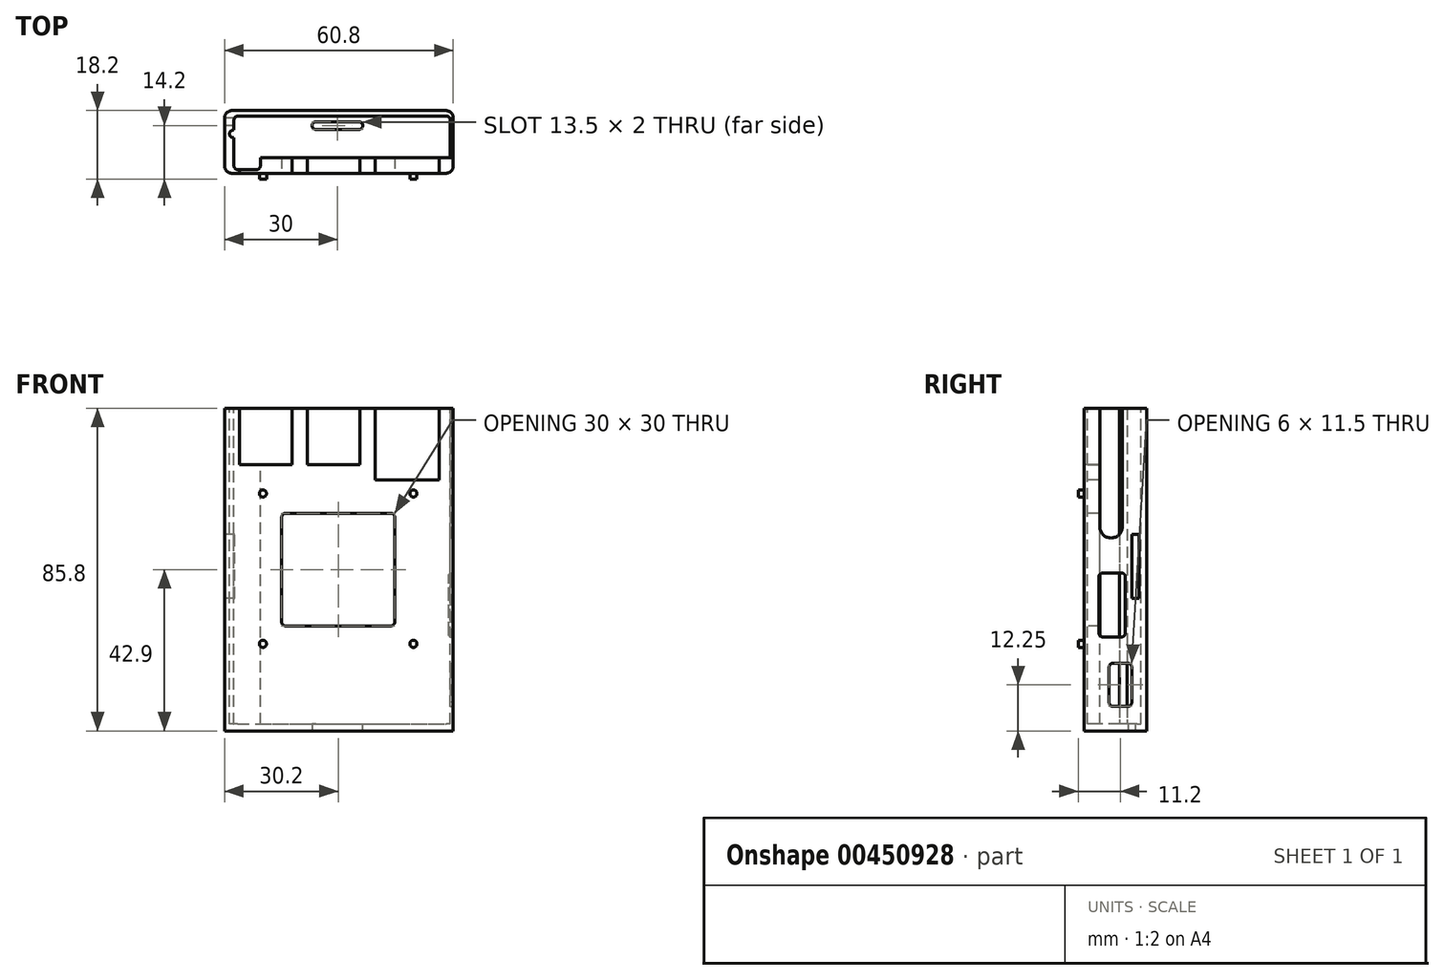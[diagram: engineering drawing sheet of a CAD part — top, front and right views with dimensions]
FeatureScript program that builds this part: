
annotation { "Feature Type Name" : "Feature", "Feature Type Description" : "" }
export const myFeature = defineFeature(function(context is Context, id is Id, definition is map)
    precondition{}
    {
        {
            var Q0;
            Q0=qCreatedBy(makeId("Top.planeOp"),FACE);
            var sketch = newSketch(context, id + "F0", { "sketchPlane" : qUnion([Q0])});
            skLineSegment(sketch, "E0.bottom", {"start": v(30.4, -8.35) * mm, "end": v(-30.4, -8.35) * mm});
            skLineSegment(sketch, "E0.top", {"start": v(30.4, 8.35) * mm, "end": v(-30.4, 8.35) * mm});
            skLineSegment(sketch, "E0.left", {"start": v(30.4, -8.35) * mm, "end": v(30.4, 8.35) * mm});
            skLineSegment(sketch, "E0.right", {"start": v(-30.4, -8.35) * mm, "end": v(-30.4, 8.35) * mm});
            skPoint(sketch, "E0.middle", {"position": v(0, 0) * mm});
            skSolve(sketch);
        }
        {
            var Q0;
            Q0=makeQuery(id+"F0.imprint","IMPRINT",FACE,{"disambiguationData":[TD([[makeQuery(id+"F0.imprint","IMPRINT",EDGE,{"derivedFrom":sQuery(id+"F0.wireOp",EDGE,"E0.bottom")}),-1.0]])]});
            extrude(context, id + "F1", {"entities" : qUnion([Q0]), "depth" : 85.8 * mm, "offsetDistance" : 25 * mm, "flatOperationType" : FlatOperationType.REMOVE, "domain" : OperationDomain.MODEL});
        }
        {
            var Q0;
            Q0=makeQuery(id+"F1.opExtrude","CAP_FACE",FACE,{"disambiguationData":[OSD([sQuery(id+"F0.wireOp",EDGE,"E0.bottom"),sQuery(id+"F0.wireOp",EDGE,"E0.top"),sQuery(id+"F0.wireOp",EDGE,"E0.left"),sQuery(id+"F0.wireOp",EDGE,"E0.right")])],"isStart":false});
            var sketch = newSketch(context, id + "F2", { "sketchPlane" : qUnion([Q0])});
            skLineSegment(sketch, "E1.bottom", {"start": v(-27.9, 6.85) * mm, "end": v(29.6, 6.85) * mm});
            skLineSegment(sketch, "E1.top", {"start": v(-27.9, -4.15) * mm, "end": v(29.6, -4.15) * mm});
            skLineSegment(sketch, "E1.left", {"start": v(-27.9, 6.85) * mm, "end": v(-27.9, -4.15) * mm});
            skLineSegment(sketch, "E1.right", {"start": v(29.6, 6.85) * mm, "end": v(29.6, -4.15) * mm});
            skSolve(sketch);
        }
        {
            var Q0;
            Q0=makeQuery(id+"F2.imprint","IMPRINT",FACE,{"disambiguationData":[TD([[makeQuery(id+"F2.imprint","IMPRINT",EDGE,{"derivedFrom":sQuery(id+"F2.wireOp",EDGE,"E1.bottom")}),-1.0]])]});
            extrude(context, id + "F3", {"entities" : qUnion([Q0]), "operationType" : NewBodyOperationType.REMOVE, "oppositeDirection" : true, "depth" : 84 * mm, "offsetDistance" : 25 * mm});
        }
        {
            var Q0;
            Q0=makeQuery(id+"F1.opExtrude","CAP_FACE",FACE,{"disambiguationData":[OSD([sQuery(id+"F0.wireOp",EDGE,"E0.bottom"),sQuery(id+"F0.wireOp",EDGE,"E0.top"),sQuery(id+"F0.wireOp",EDGE,"E0.left"),sQuery(id+"F0.wireOp",EDGE,"E0.right")])],"isStart":false});
            var sketch = newSketch(context, id + "F4", { "sketchPlane" : qUnion([Q0])});
            skLineSegment(sketch, "E2.bottom", {"start": v(-27.9, -4.15) * mm, "end": v(-20.9, -4.15) * mm});
            skLineSegment(sketch, "E2.top", {"start": v(-27.9, -7.35) * mm, "end": v(-20.9, -7.35) * mm});
            skLineSegment(sketch, "E2.left", {"start": v(-27.9, -4.15) * mm, "end": v(-27.9, -7.35) * mm});
            skLineSegment(sketch, "E2.right", {"start": v(-20.9, -4.15) * mm, "end": v(-20.9, -7.35) * mm});
            skSolve(sketch);
        }
        {
            var Q0;
            Q0 = qSketchRegion(id + "F4", true);
            extrude(context, id + "F5", {"entities" : qUnion([Q0]), "operationType" : NewBodyOperationType.REMOVE, "oppositeDirection" : true, "depth" : 84 * mm, "offsetDistance" : 25 * mm});
        }
        {
            var Q0;
            Q0=makeQuery(id+"F1.opExtrude","SWEPT_FACE",FACE,{"disambiguationData":[OSD([sQuery(id+"F0.wireOp",EDGE,"E0.bottom")])]});
            var sketch = newSketch(context, id + "F6", { "sketchPlane" : qUnion([Q0])});
            skLineSegment(sketch, "E3.bottom", {"start": v(-12.4, 70.8) * mm, "end": v(-26.4, 70.8) * mm});
            skLineSegment(sketch, "E3.top", {"start": v(-12.4, 85.8) * mm, "end": v(-26.4, 85.8) * mm});
            skLineSegment(sketch, "E3.left", {"start": v(-12.4, 70.8) * mm, "end": v(-12.4, 85.8) * mm});
            skLineSegment(sketch, "E3.right", {"start": v(-26.4, 70.8) * mm, "end": v(-26.4, 85.8) * mm});
            skPoint(sketch, "E3.middle", {"position": v(-19.4, 78.3) * mm});
            skSolve(sketch);
        }
        {
            var Q0;
            Q0=makeQuery(id+"F6.imprint","IMPRINT",FACE,{"disambiguationData":[TD([[makeQuery(id+"F6.imprint","IMPRINT",EDGE,{"derivedFrom":sQuery(id+"F6.wireOp",EDGE,"E3.bottom")}),1.0]])]});
            var sketch = newSketch(context, id + "F7", { "sketchPlane" : qUnion([Q0])});
            skLineSegment(sketch, "E4.bottom", {"start": v(5.6, 70.8) * mm, "end": v(-8.4, 70.8) * mm});
            skLineSegment(sketch, "E4.top", {"start": v(5.6, 85.8) * mm, "end": v(-8.4, 85.8) * mm});
            skLineSegment(sketch, "E4.left", {"start": v(5.6, 70.8) * mm, "end": v(5.6, 85.8) * mm});
            skLineSegment(sketch, "E4.right", {"start": v(-8.4, 70.8) * mm, "end": v(-8.4, 85.8) * mm});
            skPoint(sketch, "E4.middle", {"position": v(-1.4, 78.3) * mm});
            skSolve(sketch);
        }
        {
            var Q0;
            Q0=makeQuery(id+"F6.imprint","IMPRINT",FACE,{"disambiguationData":[TD([[makeQuery(id+"F6.imprint","IMPRINT",EDGE,{"derivedFrom":sQuery(id+"F6.wireOp",EDGE,"E3.bottom")}),1.0]])]});
            var sketch = newSketch(context, id + "F8", { "sketchPlane" : qUnion([Q0])});
            skLineSegment(sketch, "E5.bottom", {"start": v(26.6, 66.8) * mm, "end": v(9.6, 66.8) * mm});
            skLineSegment(sketch, "E5.top", {"start": v(26.6, 85.8) * mm, "end": v(9.6, 85.8) * mm});
            skLineSegment(sketch, "E5.left", {"start": v(26.6, 66.8) * mm, "end": v(26.6, 85.8) * mm});
            skLineSegment(sketch, "E5.right", {"start": v(9.6, 66.8) * mm, "end": v(9.6, 85.8) * mm});
            skPoint(sketch, "E5.middle", {"position": v(18.1, 76.3) * mm});
            skSolve(sketch);
        }
        {
            var Q0;
            Q0 = qSketchRegion(id + "F6", true);
            var Q1;
            Q1 = qSketchRegion(id + "F7", true);
            var Q2;
            Q2 = qSketchRegion(id + "F8", true);
            extrude(context, id + "F9", {"entities" : qUnion([Q0, Q1, Q2]), "operationType" : NewBodyOperationType.REMOVE, "oppositeDirection" : true, "depth" : 4.5 * mm, "offsetDistance" : 25 * mm});
        }
        {
            var Q0;
            Q0=makeQuery(id+"F1.opExtrude","SWEPT_FACE",FACE,{"disambiguationData":[OSD([sQuery(id+"F0.wireOp",EDGE,"E0.left")])]});
            var sketch = newSketch(context, id + "F10", { "sketchPlane" : qUnion([Q0])});
            skLineSegment(sketch, "E6.bottom", {"start": v(-1.65, 6.5) * mm, "end": v(4.35, 6.5) * mm});
            skLineSegment(sketch, "E6.top", {"start": v(-1.65, 18) * mm, "end": v(4.35, 18) * mm});
            skLineSegment(sketch, "E6.left", {"start": v(-1.65, 6.5) * mm, "end": v(-1.65, 18) * mm});
            skLineSegment(sketch, "E6.right", {"start": v(4.35, 6.5) * mm, "end": v(4.35, 18) * mm});
            skSolve(sketch);
        }
        {
            var Q0;
            Q0=makeQuery(id+"F10.imprint","IMPRINT",FACE,{"disambiguationData":[TD([[makeQuery(id+"F10.imprint","IMPRINT",EDGE,{"derivedFrom":sQuery(id+"F10.wireOp",EDGE,"E6.bottom")}),-1.0]])]});
            var sketch = newSketch(context, id + "F11", { "sketchPlane" : qUnion([Q0])});
            skLineSegment(sketch, "E7.bottom", {"start": v(-4.35, 25) * mm, "end": v(2.65, 25) * mm});
            skLineSegment(sketch, "E7.top", {"start": v(-4.35, 42) * mm, "end": v(2.65, 42) * mm});
            skLineSegment(sketch, "E7.left", {"start": v(-4.35, 25) * mm, "end": v(-4.35, 42) * mm});
            skLineSegment(sketch, "E7.right", {"start": v(2.65, 25) * mm, "end": v(2.65, 42) * mm});
            skSolve(sketch);
        }
        {
            var Q0;
            Q0=makeQuery(id+"F10.imprint","IMPRINT",FACE,{"disambiguationData":[TD([[makeQuery(id+"F10.imprint","IMPRINT",EDGE,{"derivedFrom":sQuery(id+"F10.wireOp",EDGE,"E6.bottom")}),-1.0]])]});
            var sketch = newSketch(context, id + "F12", { "sketchPlane" : qUnion([Q0])});
            skCircle(sketch, "E8", {"center": v(-1.15, 54.8) * mm, "radius": 2.5 * mm});
            skSolve(sketch);
        }
        {
            var Q0;
            Q0=makeQuery(id+"F3.boolean.opBoolean","COPY",FACE,{"derivedFrom":makeQuery(id+"F3.opExtrude","SWEPT_FACE",FACE,{"disambiguationData":[OSD([sQuery(id+"F2.wireOp",EDGE,"E1.right")])]})});
            var sketch = newSketch(context, id + "F13", { "sketchPlane" : qUnion([Q0])});
            skLineSegment(sketch, "E9.bottom", {"start": v(4.15, 85.8) * mm, "end": v(-1.85, 85.8) * mm});
            skLineSegment(sketch, "E9.top", {"start": v(4.15, 54.3) * mm, "end": v(-1.85, 54.3) * mm});
            skLineSegment(sketch, "E9.left", {"start": v(4.15, 85.8) * mm, "end": v(4.15, 54.3) * mm});
            skLineSegment(sketch, "E9.right", {"start": v(-1.85, 85.8) * mm, "end": v(-1.85, 54.3) * mm});
            skSolve(sketch);
        }
        {
            var Q0;
            Q0=makeQuery(id+"F13.imprint","IMPRINT",FACE,{"disambiguationData":[TD([[makeQuery(id+"F13.imprint","IMPRINT",EDGE,{"derivedFrom":sQuery(id+"F13.wireOp",EDGE,"E9.bottom")}),-1.0]])]});
            extrude(context, id + "F14", {"entities" : qUnion([Q0]), "operationType" : NewBodyOperationType.REMOVE, "oppositeDirection" : true, "depth" : 1.5 * mm, "offsetDistance" : 25 * mm});
        }
        {
            var Q0;
            Q0 = qSketchRegion(id + "F12", true);
            extrude(context, id + "F15", {"entities" : qUnion([Q0]), "operationType" : NewBodyOperationType.REMOVE, "oppositeDirection" : true, "depth" : 1.5 * mm, "offsetDistance" : 25 * mm});
        }
        {
            var Q0;
            Q0 = qSketchRegion(id + "F11", true);
            var Q1;
            Q1 = qSketchRegion(id + "F10", true);
            extrude(context, id + "F16", {"entities" : qUnion([Q0, Q1]), "operationType" : NewBodyOperationType.REMOVE, "oppositeDirection" : true, "depth" : 1.25 * mm, "offsetDistance" : 25 * mm});
        }
        {
            var Q0;
            Q0=makeQuery(id+"F3.boolean.opBoolean","COPY",FACE,{"derivedFrom":makeQuery(id+"F3.opExtrude","SWEPT_FACE",FACE,{"disambiguationData":[OSD([sQuery(id+"F2.wireOp",EDGE,"E1.right")])]})});
            var sketch = newSketch(context, id + "F17", { "sketchPlane" : qUnion([Q0])});
            skCircle(sketch, "E10", {"center": v(1.15, 54.3) * mm, "radius": 3 * mm});
            skSolve(sketch);
        }
        {
            var Q0;
            Q0 = qSketchRegion(id + "F17", true);
            extrude(context, id + "F18", {"entities" : qUnion([Q0]), "operationType" : NewBodyOperationType.REMOVE, "oppositeDirection" : true, "depth" : 1.8 * mm, "offsetDistance" : 25 * mm});
        }
        {
            var Q0;
            Q0=makeQuery(id+"F16.boolean.opBoolean","COPY",EDGE,{"derivedFrom":makeQuery(id+"F16.opExtrude","SWEPT_EDGE",EDGE,{"disambiguationData":[OSD([sQuery(id+"F11.wireOp",EDGE,"E7.bottom"),sQuery(id+"F11.wireOp",EDGE,"E7.left")])]})});
            var Q1;
            Q1=makeQuery(id+"F16.boolean.opBoolean","COPY",EDGE,{"derivedFrom":makeQuery(id+"F16.opExtrude","SWEPT_EDGE",EDGE,{"disambiguationData":[OSD([sQuery(id+"F11.wireOp",EDGE,"E7.top"),sQuery(id+"F11.wireOp",EDGE,"E7.left")])]})});
            var Q2;
            Q2=makeQuery(id+"F16.boolean.opBoolean","COPY",EDGE,{"derivedFrom":makeQuery(id+"F16.opExtrude","SWEPT_EDGE",EDGE,{"disambiguationData":[OSD([sQuery(id+"F10.wireOp",EDGE,"E6.top"),sQuery(id+"F10.wireOp",EDGE,"E6.left")])]})});
            var Q3;
            Q3=makeQuery(id+"F16.boolean.opBoolean","COPY",EDGE,{"derivedFrom":makeQuery(id+"F16.opExtrude","SWEPT_EDGE",EDGE,{"disambiguationData":[OSD([sQuery(id+"F11.wireOp",EDGE,"E7.top"),sQuery(id+"F11.wireOp",EDGE,"E7.right")])]})});
            var Q4;
            Q4=makeQuery(id+"F16.boolean.opBoolean","COPY",EDGE,{"derivedFrom":makeQuery(id+"F16.opExtrude","SWEPT_EDGE",EDGE,{"disambiguationData":[OSD([sQuery(id+"F11.wireOp",EDGE,"E7.bottom"),sQuery(id+"F11.wireOp",EDGE,"E7.right")])]})});
            var Q5;
            Q5=makeQuery(id+"F16.boolean.opBoolean","COPY",EDGE,{"derivedFrom":makeQuery(id+"F16.opExtrude","SWEPT_EDGE",EDGE,{"disambiguationData":[OSD([sQuery(id+"F10.wireOp",EDGE,"E6.top"),sQuery(id+"F10.wireOp",EDGE,"E6.right")])]})});
            var Q6;
            Q6=makeQuery(id+"F16.boolean.opBoolean","COPY",EDGE,{"derivedFrom":makeQuery(id+"F16.opExtrude","SWEPT_EDGE",EDGE,{"disambiguationData":[OSD([sQuery(id+"F10.wireOp",EDGE,"E6.bottom"),sQuery(id+"F10.wireOp",EDGE,"E6.right")])]})});
            var Q7;
            Q7=makeQuery(id+"F16.boolean.opBoolean","COPY",EDGE,{"derivedFrom":makeQuery(id+"F16.opExtrude","SWEPT_EDGE",EDGE,{"disambiguationData":[OSD([sQuery(id+"F10.wireOp",EDGE,"E6.bottom"),sQuery(id+"F10.wireOp",EDGE,"E6.left")])]})});
            fillet(context, id + "F19", {"entities" : qUnion([Q0, Q1, Q2, Q3, Q4, Q5, Q6, Q7]), "radius" : 1 * mm, "tangentPropagation" : true, "allowEdgeOverflow" : false});
        }
        {
            var Q0;
            Q0=makeQuery(id+"F1.opExtrude","SWEPT_EDGE",EDGE,{"disambiguationData":[OSD([sQuery(id+"F0.wireOp",EDGE,"E0.top"),sQuery(id+"F0.wireOp",EDGE,"E0.right")])]});
            var Q1;
            Q1=makeQuery(id+"F1.opExtrude","SWEPT_EDGE",EDGE,{"disambiguationData":[OSD([sQuery(id+"F0.wireOp",EDGE,"E0.bottom"),sQuery(id+"F0.wireOp",EDGE,"E0.right")])]});
            var Q2;
            Q2=makeQuery(id+"F1.opExtrude","SWEPT_EDGE",EDGE,{"disambiguationData":[OSD([sQuery(id+"F0.wireOp",EDGE,"E0.top"),sQuery(id+"F0.wireOp",EDGE,"E0.left")])]});
            var Q3;
            Q3=makeQuery(id+"F1.opExtrude","SWEPT_EDGE",EDGE,{"disambiguationData":[OSD([sQuery(id+"F0.wireOp",EDGE,"E0.bottom"),sQuery(id+"F0.wireOp",EDGE,"E0.left")])]});
            fillet(context, id + "F20", {"entities" : qUnion([Q0, Q1, Q2, Q3]), "radius" : 2 * mm, "tangentPropagation" : true, "allowEdgeOverflow" : false});
        }
        {
            var Q0;
            Q0=makeQuery(id+"F1.opExtrude","SWEPT_FACE",FACE,{"disambiguationData":[OSD([sQuery(id+"F0.wireOp",EDGE,"E0.right")])]});
            var sketch = newSketch(context, id + "F21", { "sketchPlane" : qUnion([Q0])});
            skLineSegment(sketch, "E11.bottom", {"start": v(-6.35, 35.3) * mm, "end": v(-4.35, 35.3) * mm});
            skLineSegment(sketch, "E11.top", {"start": v(-6.35, 52.3) * mm, "end": v(-4.35, 52.3) * mm});
            skLineSegment(sketch, "E11.left", {"start": v(-6.35, 35.3) * mm, "end": v(-6.35, 52.3) * mm});
            skLineSegment(sketch, "E11.right", {"start": v(-4.35, 35.3) * mm, "end": v(-4.35, 52.3) * mm});
            skSolve(sketch);
        }
        {
            var Q0;
            Q0=makeQuery(id+"F21.imprint","IMPRINT",FACE,{"disambiguationData":[TD([[makeQuery(id+"F21.imprint","IMPRINT",EDGE,{"derivedFrom":sQuery(id+"F21.wireOp",EDGE,"E11.bottom")}),1.0]])]});
            extrude(context, id + "F22", {"entities" : qUnion([Q0]), "operationType" : NewBodyOperationType.REMOVE, "endBound" : BoundingType.THROUGH_ALL, "oppositeDirection" : true, "depth" : 25 * mm, "offsetDistance" : 25 * mm});
        }
        {
            var Q0;
            Q0=makeQuery(id+"F5.boolean.opBoolean","MERGE",FACE,{"derivedFrom":[makeQuery(id+"F3.boolean.opBoolean","COPY",FACE,{"derivedFrom":makeQuery(id+"F3.opExtrude","SWEPT_FACE",FACE,{"disambiguationData":[OSD([sQuery(id+"F2.wireOp",EDGE,"E1.left")])]})}),makeQuery(id+"F5.opExtrude","SWEPT_FACE",FACE,{"disambiguationData":[OSD([sQuery(id+"F4.wireOp",EDGE,"E2.left")])]})]});
            var sketch = newSketch(context, id + "F23", { "sketchPlane" : qUnion([Q0])});
            skLineSegment(sketch, "E12.bottom", {"start": v(1.15, 85.8) * mm, "end": v(3.15, 85.8) * mm});
            skLineSegment(sketch, "E12.top", {"start": v(1.15, 1.8) * mm, "end": v(3.15, 1.8) * mm});
            skLineSegment(sketch, "E12.left", {"start": v(1.15, 85.8) * mm, "end": v(1.15, 1.8) * mm});
            skLineSegment(sketch, "E12.right", {"start": v(3.15, 85.8) * mm, "end": v(3.15, 1.8) * mm});
            skSolve(sketch);
        }
        {
            var Q0;
            Q0=makeQuery(id+"F23.imprint","IMPRINT",FACE,{"disambiguationData":[TD([[makeQuery(id+"F23.imprint","IMPRINT",EDGE,{"derivedFrom":sQuery(id+"F23.wireOp",EDGE,"E12.bottom")}),1.0]])]});
            extrude(context, id + "F24", {"entities" : qUnion([Q0]), "operationType" : NewBodyOperationType.REMOVE, "oppositeDirection" : true, "depth" : 1.2 * mm, "offsetDistance" : 25 * mm});
        }
        {
            var Q0;
            Q0=makeQuery(id+"F24.boolean.opBoolean","COPY",EDGE,{"derivedFrom":makeQuery(id+"F24.opExtrude","CAP_EDGE",EDGE,{"disambiguationData":[OSD([sQuery(id+"F23.wireOp",EDGE,"E12.right")])],"isStart":false})});
            var Q1;
            Q1=makeQuery(id+"F24.boolean.opBoolean","COPY",EDGE,{"derivedFrom":makeQuery(id+"F24.opExtrude","CAP_EDGE",EDGE,{"disambiguationData":[OSD([sQuery(id+"F23.wireOp",EDGE,"E12.left")])],"isStart":false})});
            fillet(context, id + "F25", {"entities" : qUnion([Q0, Q1]), "radius" : 1 * mm, "tangentPropagation" : true, "allowEdgeOverflow" : false});
        }
        {
            var Q0;
            Q0=makeQuery(id+"F1.opExtrude","SWEPT_FACE",FACE,{"disambiguationData":[OSD([sQuery(id+"F0.wireOp",EDGE,"E0.bottom")])]});
            var sketch = newSketch(context, id + "F26", { "sketchPlane" : qUnion([Q0])});
            skLineSegment(sketch, "E13.bottom", {"start": v(14.8, 27.9) * mm, "end": v(-15.2, 27.9) * mm});
            skLineSegment(sketch, "E13.top", {"start": v(14.8, 57.9) * mm, "end": v(-15.2, 57.9) * mm});
            skLineSegment(sketch, "E13.left", {"start": v(14.8, 27.9) * mm, "end": v(14.8, 57.9) * mm});
            skLineSegment(sketch, "E13.right", {"start": v(-15.2, 27.9) * mm, "end": v(-15.2, 57.9) * mm});
            skPoint(sketch, "E13.middle", {"position": v(-0.2, 42.9) * mm});
            skSolve(sketch);
        }
        {
            var Q0;
            Q0 = qSketchRegion(id + "F26", true);
            extrude(context, id + "F27", {"entities" : qUnion([Q0]), "operationType" : NewBodyOperationType.REMOVE, "oppositeDirection" : true, "depth" : 5 * mm, "offsetDistance" : 25 * mm});
        }
        {
            var Q0;
            Q0=makeQuery(id+"F1.opExtrude","SWEPT_FACE",FACE,{"disambiguationData":[OSD([sQuery(id+"F0.wireOp",EDGE,"E0.bottom")])]});
            var sketch = newSketch(context, id + "F28", { "sketchPlane" : qUnion([Q0])});
            skLineSegment(sketch, "E14.bottom", {"start": v(19.8, 23.14) * mm, "end": v(-20.2, 23.14) * mm});
            skLineSegment(sketch, "E14.top", {"start": v(19.8, 63.14) * mm, "end": v(-20.2, 63.14) * mm});
            skLineSegment(sketch, "E14.left", {"start": v(19.8, 23.14) * mm, "end": v(19.8, 63.14) * mm});
            skLineSegment(sketch, "E14.right", {"start": v(-20.2, 23.14) * mm, "end": v(-20.2, 63.14) * mm});
            skPoint(sketch, "E14.middle", {"position": v(-0.2, 43.14) * mm});
            skPoint(sketch, "E14.middle.positionSnap0", {"position": v(-0.2, 27.9) * mm});
            skPoint(sketch, "E14.centerSnap0", {"position": v(-0.2, 27.9) * mm});
            skSolve(sketch);
        }
        {
            var Q0;
            Q0=makeQuery(id+"F28.imprint","IMPRINT",FACE,{"disambiguationData":[TD([[makeQuery(id+"F28.imprint","IMPRINT",EDGE,{"derivedFrom":sQuery(id+"F28.wireOp",EDGE,"E14.bottom")}),1.0]])]});
            var sketch = newSketch(context, id + "F29", { "sketchPlane" : qUnion([Q0])});
            skCircle(sketch, "E15", {"center": v(-20.2, 63.14) * mm, "radius": 0.95 * mm});
            skCircle(sketch, "E16", {"center": v(19.8, 63.14) * mm, "radius": 0.95 * mm});
            skCircle(sketch, "E17", {"center": v(19.8, 23.14) * mm, "radius": 0.95 * mm});
            skCircle(sketch, "E18", {"center": v(-20.2, 23.14) * mm, "radius": 0.95 * mm});
            skSolve(sketch);
        }
        {
            var Q0;
            Q0 = qSketchRegion(id + "F29", true);
            extrude(context, id + "F30", {"entities" : qUnion([Q0]), "flatOperationType" : FlatOperationType.REMOVE, "depth" : 1.5 * mm, "offsetDistance" : 25 * mm, "domain" : OperationDomain.MODEL});
        }
        {
            var Q0;
            Q0=makeQuery(id+"F1.opExtrude","CAP_FACE",FACE,{"disambiguationData":[OSD([sQuery(id+"F0.wireOp",EDGE,"E0.bottom"),sQuery(id+"F0.wireOp",EDGE,"E0.top"),sQuery(id+"F0.wireOp",EDGE,"E0.left"),sQuery(id+"F0.wireOp",EDGE,"E0.right")])],"isStart":true});
            var sketch = newSketch(context, id + "F31", { "sketchPlane" : qUnion([Q0])});
            skLineSegment(sketch, "E19.bottom", {"start": v(6.35, -5.35) * mm, "end": v(-7.15, -5.35) * mm});
            skLineSegment(sketch, "E19.top", {"start": v(6.35, -3.35) * mm, "end": v(-7.15, -3.35) * mm});
            skLineSegment(sketch, "E19.left", {"start": v(6.35, -5.35) * mm, "end": v(6.35, -3.35) * mm});
            skLineSegment(sketch, "E19.right", {"start": v(-7.15, -5.35) * mm, "end": v(-7.15, -3.35) * mm});
            skPoint(sketch, "E19.middle", {"position": v(-0.4, -4.35) * mm});
            skSolve(sketch);
        }
        {
            var Q0;
            Q0 = qSketchRegion(id + "F31", true);
            extrude(context, id + "F32", {"entities" : qUnion([Q0]), "operationType" : NewBodyOperationType.REMOVE, "oppositeDirection" : true, "depth" : 2 * mm, "offsetDistance" : 25 * mm});
        }
        {
            var Q0;
            Q0=makeQuery(id+"F5.boolean.opBoolean","COPY",EDGE,{"derivedFrom":makeQuery(id+"F5.opExtrude","SWEPT_EDGE",EDGE,{"disambiguationData":[OSD([sQuery(id+"F2.wireOp",EDGE,"E1.top"),sQuery(id+"F4.wireOp",EDGE,"E2.bottom"),sQuery(id+"F4.wireOp",EDGE,"E2.right")])]})});
            var Q1;
            Q1=makeQuery(id+"F5.boolean.opBoolean","COPY",EDGE,{"derivedFrom":makeQuery(id+"F5.opExtrude","SWEPT_EDGE",EDGE,{"disambiguationData":[OSD([sQuery(id+"F4.wireOp",EDGE,"E2.top"),sQuery(id+"F4.wireOp",EDGE,"E2.right")])]})});
            var Q2;
            Q2=makeQuery(id+"F5.boolean.opBoolean","COPY",EDGE,{"derivedFrom":makeQuery(id+"F5.opExtrude","SWEPT_EDGE",EDGE,{"disambiguationData":[OSD([sQuery(id+"F4.wireOp",EDGE,"E2.top"),sQuery(id+"F4.wireOp",EDGE,"E2.left")])]})});
            var Q3;
            Q3=makeQuery(id+"F3.boolean.opBoolean","COPY",EDGE,{"derivedFrom":makeQuery(id+"F3.opExtrude","SWEPT_EDGE",EDGE,{"disambiguationData":[OSD([sQuery(id+"F2.wireOp",EDGE,"E1.bottom"),sQuery(id+"F2.wireOp",EDGE,"E1.left")])]})});
            var Q4;
            Q4=makeQuery(id+"F3.boolean.opBoolean","COPY",EDGE,{"derivedFrom":makeQuery(id+"F3.opExtrude","SWEPT_EDGE",EDGE,{"disambiguationData":[OSD([sQuery(id+"F2.wireOp",EDGE,"E1.bottom"),sQuery(id+"F2.wireOp",EDGE,"E1.right")])]})});
            var Q5;
            Q5=makeQuery(id+"F27.boolean.opBoolean","COPY",EDGE,{"derivedFrom":makeQuery(id+"F27.opExtrude","SWEPT_EDGE",EDGE,{"disambiguationData":[OSD([sQuery(id+"F26.wireOp",EDGE,"E13.top"),sQuery(id+"F26.wireOp",EDGE,"E13.right")])]})});
            var Q6;
            Q6=makeQuery(id+"F27.boolean.opBoolean","COPY",EDGE,{"derivedFrom":makeQuery(id+"F27.opExtrude","SWEPT_EDGE",EDGE,{"disambiguationData":[OSD([sQuery(id+"F26.wireOp",EDGE,"E13.bottom"),sQuery(id+"F26.wireOp",EDGE,"E13.right")])]})});
            var Q7;
            Q7=makeQuery(id+"F27.boolean.opBoolean","COPY",EDGE,{"derivedFrom":makeQuery(id+"F27.opExtrude","SWEPT_EDGE",EDGE,{"disambiguationData":[OSD([sQuery(id+"F26.wireOp",EDGE,"E13.top"),sQuery(id+"F26.wireOp",EDGE,"E13.left")])]})});
            var Q8;
            Q8=makeQuery(id+"F27.boolean.opBoolean","COPY",EDGE,{"derivedFrom":makeQuery(id+"F27.opExtrude","SWEPT_EDGE",EDGE,{"disambiguationData":[OSD([sQuery(id+"F26.wireOp",EDGE,"E13.bottom"),sQuery(id+"F26.wireOp",EDGE,"E13.left")])]})});
            var Q9;
            Q9=makeQuery(id+"F32.boolean.opBoolean","COPY",EDGE,{"derivedFrom":makeQuery(id+"F32.opExtrude","SWEPT_EDGE",EDGE,{"disambiguationData":[OSD([sQuery(id+"F31.wireOp",EDGE,"E19.top"),sQuery(id+"F31.wireOp",EDGE,"E19.left")])]})});
            var Q10;
            Q10=makeQuery(id+"F32.boolean.opBoolean","COPY",EDGE,{"derivedFrom":makeQuery(id+"F32.opExtrude","SWEPT_EDGE",EDGE,{"disambiguationData":[OSD([sQuery(id+"F31.wireOp",EDGE,"E19.top"),sQuery(id+"F31.wireOp",EDGE,"E19.right")])]})});
            var Q11;
            Q11=makeQuery(id+"F32.boolean.opBoolean","COPY",EDGE,{"derivedFrom":makeQuery(id+"F32.opExtrude","SWEPT_EDGE",EDGE,{"disambiguationData":[OSD([sQuery(id+"F31.wireOp",EDGE,"E19.bottom"),sQuery(id+"F31.wireOp",EDGE,"E19.right")])]})});
            var Q12;
            Q12=makeQuery(id+"F32.boolean.opBoolean","COPY",EDGE,{"derivedFrom":makeQuery(id+"F32.opExtrude","SWEPT_EDGE",EDGE,{"disambiguationData":[OSD([sQuery(id+"F31.wireOp",EDGE,"E19.bottom"),sQuery(id+"F31.wireOp",EDGE,"E19.left")])]})});
            fillet(context, id + "F33", {"entities" : qUnion([Q0, Q1, Q2, Q3, Q4, Q5, Q6, Q7, Q8, Q9, Q10, Q11, Q12]), "radius" : 1 * mm, "tangentPropagation" : true, "allowEdgeOverflow" : false});
        }
    });
